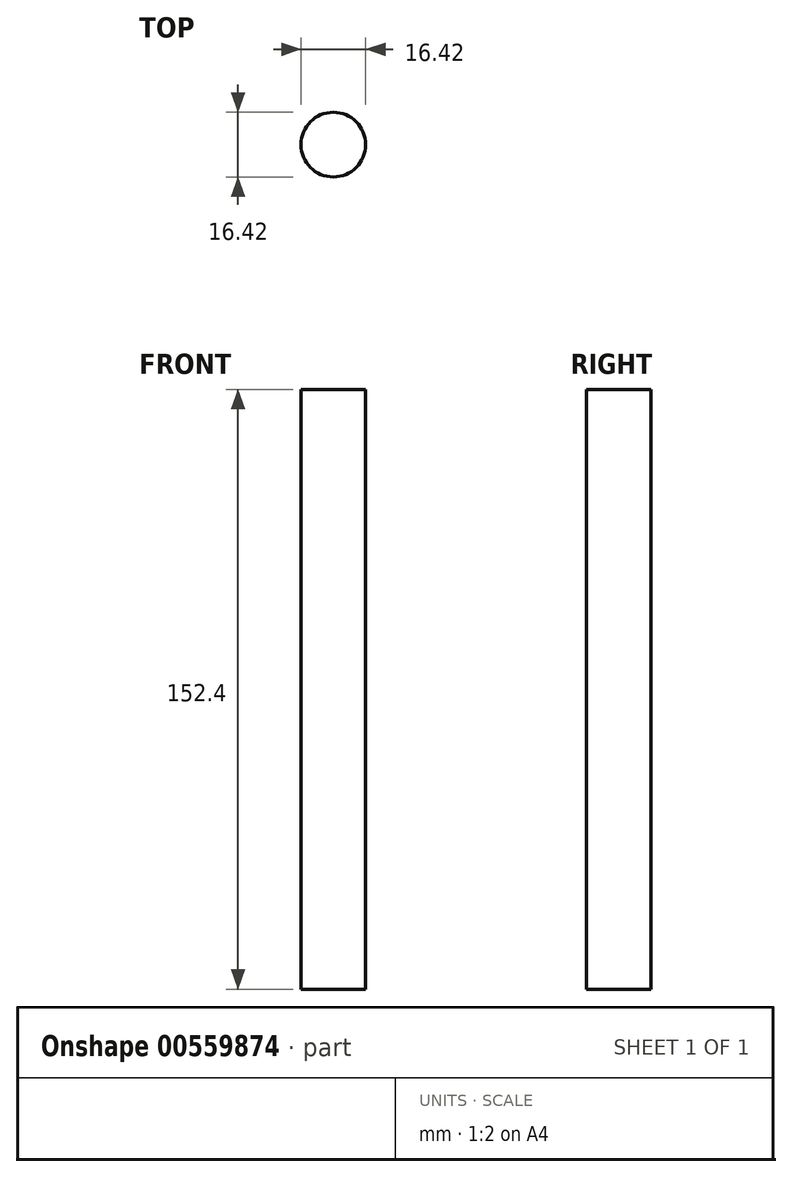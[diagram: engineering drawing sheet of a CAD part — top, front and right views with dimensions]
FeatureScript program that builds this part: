
annotation { "Feature Type Name" : "Feature", "Feature Type Description" : "" }
export const myFeature = defineFeature(function(context is Context, id is Id, definition is map)
    precondition{}
    {
        {
            var Q0;
            Q0=qCreatedBy(makeId("Front.planeOp"),FACE);
            var sketch = newSketch(context, id + "F0", { "sketchPlane" : qUnion([Q0])});
            skFitSpline(sketch, "E0", {"points": [v(-37.3, 64.67) * mm, v(-65.57, 25.27) * mm, v(-20.75, -15.34) * mm, v(-12.93, -37) * mm, v(-12.93, -50.23) * mm], "startDerivative": vector(-160.14, -132.86) * mm, "endDerivative": vector(-1.24, -80.32) * mm});
            skLineSegment(sketch, "E1", {"start": v(0, 69.48) * mm, "end": v(0, 0) * mm});
            skSolve(sketch);
        }
        {
            var Q0;
            Q0 = qSketchRegion(id + "F0", true);
            var Q1;
            Q1=sQuery(id+"F0.wireOp",EDGE,"E0");
            var Q2;
            Q2=sQuery(id+"F0.wireOp",EDGE,"E1");
            revolve(context, id + "F1", {"bodyType" : ToolBodyType.SURFACE, "entities" : qUnion([Q0]), "surfaceEntities" : qUnion([Q1]), "axis" : qUnion([Q2]), "revolveType" : RevolveType.FULL});
        }
        {
            var Q0;
            Q0=qCreatedBy(makeId("Top.planeOp"),FACE);
            var sketch = newSketch(context, id + "F2", { "sketchPlane" : qUnion([Q0])});
            skCircle(sketch, "E2", {"center": v(0, 0) * mm, "radius": 8.2 * mm});
            skSolve(sketch);
        }
        {
            var Q0;
            Q0=makeQuery(id+"F2.imprint","IMPRINT",FACE,{"disambiguationData":[TD([[makeQuery(id+"F2.imprint","IMPRINT",EDGE,{"derivedFrom":sQuery(id+"F2.wireOp",EDGE,"E2")}),1.0]])]});
            extrude(context, id + "F3", {"entities" : qUnion([Q0]), "depth" : 76.2 * mm, "offsetDistance" : 25.4 * mm, "hasSecondDirection" : true, "secondDirectionOppositeDirection" : true, "secondDirectionDepth" : 76.2 * mm});
        }
    });
